# Revit family: DAL_A3-Double-Offset-1
name_source: partatom
category: Doors
revit_build: Autodesk Revit 2016 (Build: 20150220_1215(x64)
units: mm (PartAtom-declared; Revit-internal decimal feet)

## family parameters
Always vertical = Yes
Cut with Voids When Loaded = No
Host = Wall
Room Calculation Point = No
Shared = No

## types (6) — shared parameters
Architrave Setback = 5 mm  [stored 0.0164042 ft]
Door Panel Height = 2060 mm
Door Panel Thickness = 32 mm  [stored 0.104987 ft]
Frame Thickness = 32 mm  [stored 0.104987 ft]
Function = Interior
Handle Length = 350 mm  [stored 1.14829 ft]
Handle Style = UK_Handle Style F
Handle X Distance = 75 mm
Handle Z Distance = 1000 mm  [stored 3.28084 ft]
Height = 2110 mm  [stored 6.92257 ft]
Material Architrave = Door - Architrave
Material Door = Door - Panel
Material Frame = Door - Frame/Mullion
Material Ironmongery = Door - Handle
Operation = UserDefined
Rough Height = 2110 mm  [stored 6.92257 ft]
Stop Depth = 32 mm  [stored 0.104987 ft]
Stop Thickness = 19 mm  [stored 0.062336 ft]
Structural Tolerance = 8 mm  [stored 0.0262467 ft]
Thickness = 32 mm  [stored 0.104987 ft]
Tolerance = 3 mm  [stored 0.00984252 ft]
UnderCut = 7 mm  [stored 0.0229659 ft]
Vis - Ironmongery = Yes
Wall Closure = By host
zero-valued in all types: Door Panel Offset

## per-type parameters (varying)
| type | Main Panel Width | Rough Width | Secondary Panel Width | Vis - Stops | Vis - Swing Double | Vis - Swing Opposing | Vis - Swing Single | Width |
| 1510 x 2110mm Sgl Swing | 926 mm  [stored 3.03806 ft] | 1510 mm  [stored 4.95407 ft] | 495 mm  [stored 1.62402 ft] | Yes | No | No | Yes | 1510 mm  [stored 4.95407 ft] |
| 1210 x 2110mm Sgl Swing | 826 mm  [stored 2.70997 ft] | 1210 mm  [stored 3.96982 ft] | 295 mm  [stored 0.967848 ft] | Yes | No | No | Yes | 1210 mm  [stored 3.96982 ft] |
| 1210 x 2110mm Dbl Swing | 826 mm  [stored 2.70997 ft] | 1210 mm  [stored 3.96982 ft] | 295 mm  [stored 0.967848 ft] | No | Yes | No | Yes | 1210 mm  [stored 3.96982 ft] |
| 1510 x 2110mm Dbl Swing | 926 mm  [stored 3.03806 ft] | 1510 mm  [stored 4.95407 ft] | 495 mm  [stored 1.62402 ft] | No | Yes | No | Yes | 1510 mm  [stored 4.95407 ft] |
| 1510 x 2110mm Opp Swing | 926 mm  [stored 3.03806 ft] | 1510 mm  [stored 4.95407 ft] | 495 mm  [stored 1.62402 ft] | No | No | Yes | No | 1510 mm  [stored 4.95407 ft] |
| 1210 x 2110mm Opp Swing | 826 mm  [stored 2.70997 ft] | 1210 mm  [stored 3.96982 ft] | 295 mm  [stored 0.967848 ft] | No | No | Yes | No | 1210 mm  [stored 3.96982 ft] |

note: [stored X ft] marks values corroborated as IEEE doubles in the binary element streams (Revit-internal decimal feet)

## geometry (parser evidence)
native form markers: Sweep x4
no freeform markers — native parametric forms only
